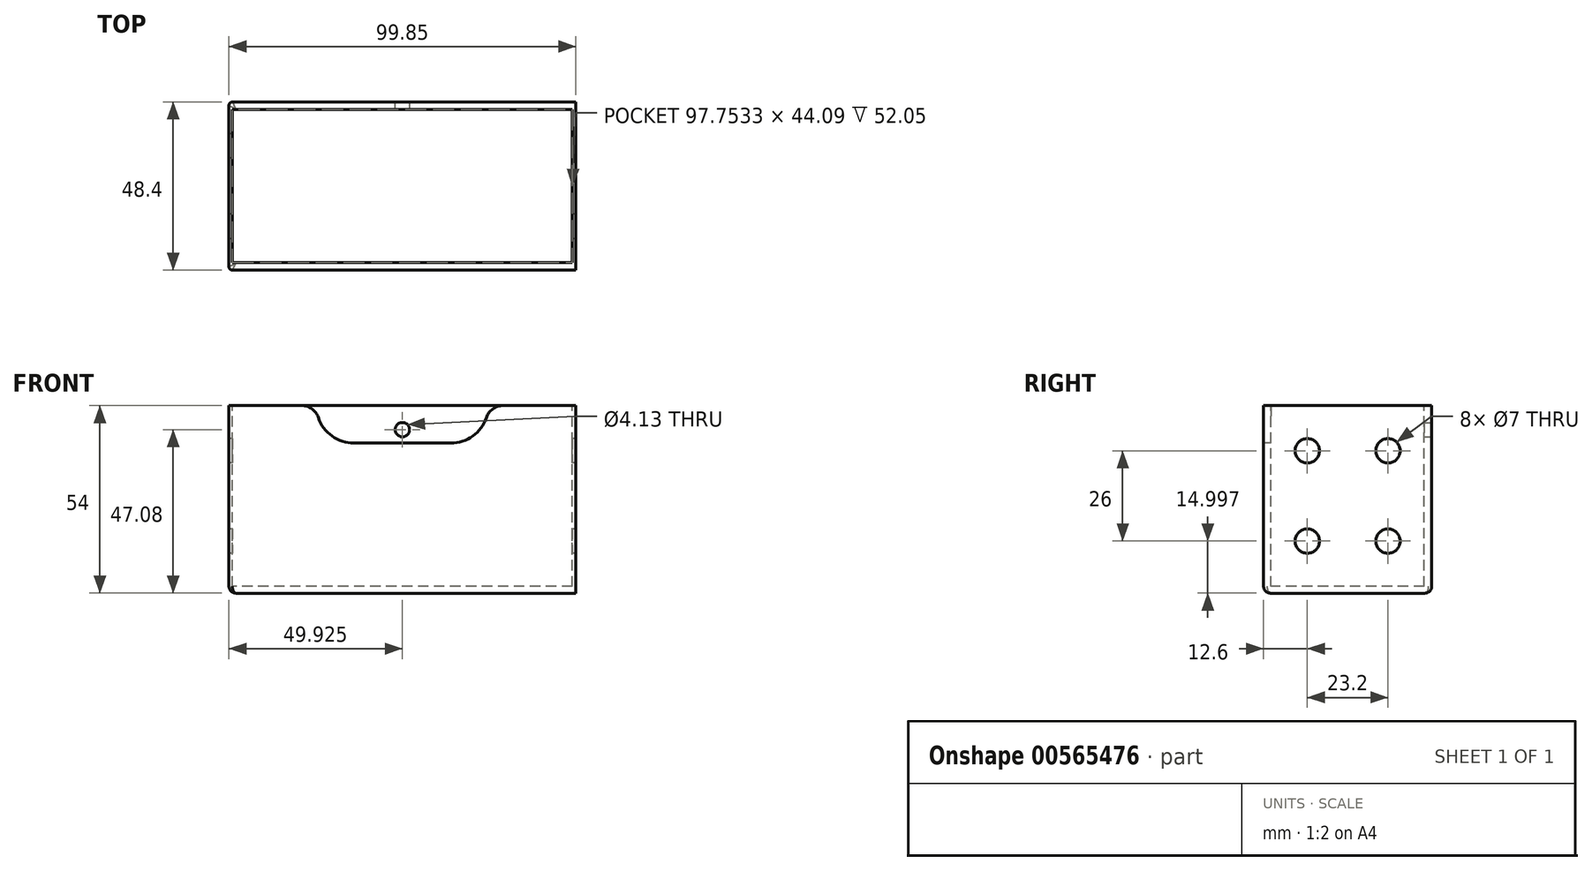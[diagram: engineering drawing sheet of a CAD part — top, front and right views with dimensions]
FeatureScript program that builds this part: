
annotation { "Feature Type Name" : "Feature", "Feature Type Description" : "" }
export const myFeature = defineFeature(function(context is Context, id is Id, definition is map)
    precondition{}
    {
        {
            var Q0;
            Q0=qCreatedBy(makeId("Front.planeOp"),FACE);
            var sketch = newSketch(context, id + "F0", { "sketchPlane" : qUnion([Q0])});
            skLineSegment(sketch, "E0.bottom", {"start": v(-48.42, 19.38) * mm, "end": v(51.43, 19.38) * mm});
            skLineSegment(sketch, "E0.top", {"start": v(-48.42, -34.62) * mm, "end": v(51.43, -34.62) * mm});
            skLineSegment(sketch, "E0.left", {"start": v(-48.42, 19.38) * mm, "end": v(-48.42, -34.62) * mm});
            skLineSegment(sketch, "E0.right", {"start": v(51.43, 19.38) * mm, "end": v(51.43, -34.62) * mm});
            skSolve(sketch);
        }
        {
            var Q0;
            Q0=makeQuery(id+"F0.imprint","IMPRINT",FACE,{"disambiguationData":[TD([[makeQuery(id+"F0.imprint","IMPRINT",EDGE,{"derivedFrom":sQuery(id+"F0.wireOp",EDGE,"E0.bottom")}),-1.0]])]});
            extrude(context, id + "F1", {"entities" : qUnion([Q0]), "depth" : (43.4 + 2 + 2 + 1) * mm, "offsetDistance" : 25 * mm});
        }
        {
            var Q0;
            Q0=makeQuery(id+"F1.opExtrude","SWEPT_FACE",FACE,{"disambiguationData":[OSD([sQuery(id+"F0.wireOp",EDGE,"E0.bottom")])]});
            var sketch = newSketch(context, id + "F2", { "sketchPlane" : qUnion([Q0])});
            skLineSegment(sketch, "E1.bottom", {"start": v(50.38, -2.15) * mm, "end": v(-47.37, -2.16) * mm});
            skLineSegment(sketch, "E1.top", {"start": v(50.38, -46.24) * mm, "end": v(-47.37, -46.25) * mm});
            skLineSegment(sketch, "E1.left", {"start": v(50.38, -2.15) * mm, "end": v(50.38, -46.24) * mm});
            skLineSegment(sketch, "E1.right", {"start": v(-47.37, -2.16) * mm, "end": v(-47.37, -46.25) * mm});
            skSolve(sketch);
        }
        {
            var Q0;
            Q0=makeQuery(id+"F1.opExtrude","SWEPT_FACE",FACE,{"disambiguationData":[OSD([sQuery(id+"F0.wireOp",EDGE,"E0.right")])]});
            extrude(context, id + "F3", {"entities" : qUnion([Q0]), "operationType" : NewBodyOperationType.ADD, "depth" : 1 * mm, "offsetDistance" : 25 * mm});
        }
        {
            var Q0;
            Q0=makeQuery(id+"F3.opExtrude","CAP_FACE",FACE,{"disambiguationData":[OSD([sQuery(id+"F0.wireOp",EDGE,"E0.right")])],"isStart":false});
            extrude(context, id + "F4", {"entities" : qUnion([Q0]), "operationType" : NewBodyOperationType.REMOVE, "oppositeDirection" : true, "depth" : 1 * mm, "offsetDistance" : 25 * mm});
        }
        {
            var Q0;
            Q0=makeQuery(id+"F2.imprint","IMPRINT",FACE,{"disambiguationData":[TD([[makeQuery(id+"F2.imprint","IMPRINT",EDGE,{"derivedFrom":sQuery(id+"F2.wireOp",EDGE,"E1.bottom")}),1.0]])]});
            extrude(context, id + "F5", {"entities" : qUnion([Q0]), "operationType" : NewBodyOperationType.REMOVE, "oppositeDirection" : true, "depth" : 52.05 * mm, "offsetDistance" : 25 * mm});
        }
        {
            var Q0;
            {var subQ0=sQuery(id+"F0.wireOp",EDGE,"E0.right");Q0=makeQuery(id+"F4.boolean.opBoolean","COPY",EDGE,{"derivedFrom":makeQuery(id+"F4.opExtrude","CAP_EDGE",EDGE,{"disambiguationData":[OSD([subQ0]),TDD([makeQuery(id+"F3.opExtrude","CAP_EDGE",EDGE,{"disambiguationData":[OSD([subQ0]),TDD([makeQuery(id+"F1.opExtrude","CAP_EDGE",EDGE,{"disambiguationData":[OSD([subQ0])],"isStart":false})])],"isStart":false})])],"isStart":false})});}
            var Q1;
            {var subQ0=sQuery(id+"F0.wireOp",EDGE,"E0.right");Q1=makeQuery(id+"F4.boolean.opBoolean","COPY",EDGE,{"derivedFrom":makeQuery(id+"F4.opExtrude","CAP_EDGE",EDGE,{"disambiguationData":[OSD([subQ0]),TDD([makeQuery(id+"F3.opExtrude","CAP_EDGE",EDGE,{"disambiguationData":[OSD([subQ0]),TDD([makeQuery(id+"F1.opExtrude","CAP_EDGE",EDGE,{"disambiguationData":[OSD([subQ0])],"isStart":true})])],"isStart":false})])],"isStart":false})});}
            var Q2;
            Q2=makeQuery(id+"F1.opExtrude","CAP_EDGE",EDGE,{"disambiguationData":[OSD([sQuery(id+"F0.wireOp",EDGE,"E0.left")])],"isStart":true});
            var Q3;
            Q3=makeQuery(id+"F1.opExtrude","CAP_EDGE",EDGE,{"disambiguationData":[OSD([sQuery(id+"F0.wireOp",EDGE,"E0.left")])],"isStart":false});
            fillet(context, id + "F6", {"entities" : qUnion([Q0, Q1, Q2, Q3]), "radius" : 1 * mm, "tangentPropagation" : true, "allowEdgeOverflow" : false});
        }
        {
            var Q0;
            {var subQ0=sQuery(id+"F0.wireOp",EDGE,"E0.right");var subQ1=sQuery(id+"F0.wireOp",EDGE,"E0.top");Q0=makeQuery(id+"F3.boolean.opBoolean","MERGE",EDGE,{"derivedFrom":[makeQuery(id+"F1.opExtrude","CAP_EDGE",EDGE,{"disambiguationData":[OSD([subQ1])],"isStart":false}),makeQuery(id+"F3.opExtrude","SWEPT_EDGE",EDGE,{"disambiguationData":[OSD([subQ1,subQ0]),TDD([makeQuery(id+"F1.opExtrude","CAP_VERTEX",VERTEX,{"disambiguationData":[OSD([subQ1,subQ0])],"isStart":false})])]})]});}
            var Q1;
            Q1=makeQuery(id+"F1.opExtrude","SWEPT_EDGE",EDGE,{"disambiguationData":[OSD([sQuery(id+"F0.wireOp",EDGE,"E0.top"),sQuery(id+"F0.wireOp",EDGE,"E0.left")])]});
            var Q2;
            {var subQ0=sQuery(id+"F0.wireOp",EDGE,"E0.right");var subQ1=sQuery(id+"F0.wireOp",EDGE,"E0.top");Q2=makeQuery(id+"F3.boolean.opBoolean","MERGE",EDGE,{"derivedFrom":[makeQuery(id+"F1.opExtrude","CAP_EDGE",EDGE,{"disambiguationData":[OSD([subQ1])],"isStart":true}),makeQuery(id+"F3.opExtrude","SWEPT_EDGE",EDGE,{"disambiguationData":[OSD([subQ1,subQ0]),TDD([makeQuery(id+"F1.opExtrude","CAP_VERTEX",VERTEX,{"disambiguationData":[OSD([subQ1,subQ0])],"isStart":true})])]})]});}
            var Q3;
            Q3=makeQuery(id+"F4.boolean.opBoolean","COPY",EDGE,{"derivedFrom":makeQuery(id+"F4.opExtrude","CAP_EDGE",EDGE,{"disambiguationData":[OSD([sQuery(id+"F0.wireOp",EDGE,"E0.top"),sQuery(id+"F0.wireOp",EDGE,"E0.right")])],"isStart":false})});
            fillet(context, id + "F7", {"entities" : qUnion([Q0, Q1, Q2, Q3]), "radius" : 2 * mm, "tangentPropagation" : true, "allowEdgeOverflow" : false});
        }
        {
            var Q0;
            {var subQ0=sQuery(id+"F0.wireOp",EDGE,"E0.right");Q0=makeQuery(id+"F3.boolean.opBoolean","MERGE",FACE,{"derivedFrom":[makeQuery(id+"F1.opExtrude","CAP_FACE",FACE,{"disambiguationData":[OSD([sQuery(id+"F0.wireOp",EDGE,"E0.bottom"),sQuery(id+"F0.wireOp",EDGE,"E0.top"),sQuery(id+"F0.wireOp",EDGE,"E0.left"),subQ0])],"isStart":false}),makeQuery(id+"F3.opExtrude","SWEPT_FACE",FACE,{"disambiguationData":[OSD([subQ0]),TDD([makeQuery(id+"F1.opExtrude","CAP_EDGE",EDGE,{"disambiguationData":[OSD([subQ0])],"isStart":false})])]})]});}
            var sketch = newSketch(context, id + "F8", { "sketchPlane" : qUnion([Q0])});
            skLineSegment(sketch, "E2", {"start": v(-47.42, 19.38) * mm, "end": v(50.43, 19.38) * mm});
            skCircle(sketch, "E3", {"center": v(-12.42, 19.38) * mm, "radius": 10.82 * mm});
            skCircle(sketch, "E4", {"center": v(15.43, 19.38) * mm, "radius": 10.82 * mm});
            skLineSegment(sketch, "E5", {"start": v(-12.42, 19.38) * mm, "end": v(-12.42, 8.56) * mm});
            skLineSegment(sketch, "E6", {"start": v(-12.42, 8.56) * mm, "end": v(15.43, 8.56) * mm});
            skLineSegment(sketch, "E7", {"start": v(15.43, 8.56) * mm, "end": v(15.43, 19.38) * mm});
            skSolve(sketch);
        }
        {
            var Q0;
            {var subQ0=sQuery(id+"F8.wireOp",EDGE,"E2");var subQ1=makeQuery(id+"F8.imprint","INTERSECT",VERTEX,{"derivedFrom":[subQ0,sQuery(id+"F8.wireOp",EDGE,"E5")]});Q0=makeQuery(id+"F8.imprint","IMPRINT",FACE,{"disambiguationData":[TD([[makeQuery(id+"F8.imprint","IMPRINT",EDGE,{"disambiguationData":[TD([[subQ1,1.0]])],"derivedFrom":subQ0}),1.0]])]});}
            var Q1;
            {var subQ0=sQuery(id+"F8.wireOp",EDGE,"E5");Q1=makeQuery(id+"F8.imprint","IMPRINT",FACE,{"disambiguationData":[TD([[makeQuery(id+"F8.imprint","IMPRINT",EDGE,{"derivedFrom":subQ0}),-1.0]])]});}
            var Q2;
            {var subQ0=sQuery(id+"F8.wireOp",EDGE,"E5");Q2=makeQuery(id+"F8.imprint","IMPRINT",FACE,{"disambiguationData":[TD([[makeQuery(id+"F8.imprint","IMPRINT",EDGE,{"derivedFrom":subQ0}),1.0]])]});}
            var Q3;
            {var subQ5=sQuery(id+"F8.wireOp",EDGE,"E6");Q3=makeQuery(id+"F8.imprint","IMPRINT",FACE,{"disambiguationData":[TD([[makeQuery(id+"F8.imprint","IMPRINT",EDGE,{"derivedFrom":subQ5}),1.0]])]});}
            var Q4;
            {var subQ0=sQuery(id+"F8.wireOp",EDGE,"E7");Q4=makeQuery(id+"F8.imprint","IMPRINT",FACE,{"disambiguationData":[TD([[makeQuery(id+"F8.imprint","IMPRINT",EDGE,{"derivedFrom":subQ0}),1.0]])]});}
            var Q5;
            {var subQ0=sQuery(id+"F8.wireOp",EDGE,"E7");Q5=makeQuery(id+"F8.imprint","IMPRINT",FACE,{"disambiguationData":[TD([[makeQuery(id+"F8.imprint","IMPRINT",EDGE,{"derivedFrom":subQ0}),-1.0]])]});}
            var Q6;
            {var subQ0=sQuery(id+"F8.wireOp",EDGE,"E2");var subQ1=makeQuery(id+"F8.imprint","INTERSECT",VERTEX,{"derivedFrom":[subQ0,sQuery(id+"F8.wireOp",EDGE,"E7")]});Q6=makeQuery(id+"F8.imprint","IMPRINT",FACE,{"disambiguationData":[TD([[makeQuery(id+"F8.imprint","IMPRINT",EDGE,{"disambiguationData":[TD([[subQ1,1.0]])],"derivedFrom":subQ0}),1.0]])]});}
            extrude(context, id + "F9", {"entities" : qUnion([Q0, Q1, Q2, Q3, Q4, Q5, Q6]), "operationType" : NewBodyOperationType.REMOVE, "oppositeDirection" : true, "depth" : 25 * mm, "offsetDistance" : 25 * mm});
        }
        {
            var Q0;
            {var subQ0=sQuery(id+"F0.wireOp",EDGE,"E0.right");Q0=makeQuery(id+"F3.boolean.opBoolean","MERGE",FACE,{"derivedFrom":[makeQuery(id+"F1.opExtrude","CAP_FACE",FACE,{"disambiguationData":[OSD([sQuery(id+"F0.wireOp",EDGE,"E0.bottom"),sQuery(id+"F0.wireOp",EDGE,"E0.top"),sQuery(id+"F0.wireOp",EDGE,"E0.left"),subQ0])],"isStart":true}),makeQuery(id+"F3.opExtrude","SWEPT_FACE",FACE,{"disambiguationData":[OSD([subQ0]),TDD([makeQuery(id+"F1.opExtrude","CAP_EDGE",EDGE,{"disambiguationData":[OSD([subQ0])],"isStart":true})])]})]});}
            var sketch = newSketch(context, id + "F10", { "sketchPlane" : qUnion([Q0])});
            skCircle(sketch, "E8", {"center": v(-1.5, 12.46) * mm, "radius": 2.06 * mm});
            skPoint(sketch, "E8.centerSnap0", {"position": v(-1.5, 19.38) * mm});
            skSolve(sketch);
        }
        {
            var Q0;
            Q0 = qSketchRegion(id + "F10", true);
            extrude(context, id + "F11", {"entities" : qUnion([Q0]), "operationType" : NewBodyOperationType.REMOVE, "oppositeDirection" : true, "depth" : 25 * mm, "offsetDistance" : 25 * mm});
        }
        {
            var Q0;
            Q0=makeQuery(id+"F1.opExtrude","SWEPT_FACE",FACE,{"disambiguationData":[OSD([sQuery(id+"F0.wireOp",EDGE,"E0.left")])]});
            var sketch = newSketch(context, id + "F12", { "sketchPlane" : qUnion([Q0])});
            skLineSegment(sketch, "E9", {"start": v(47.4, -32.62) * mm, "end": v(47.4, 19.38) * mm});
            skCircle(sketch, "E10", {"center": v(12.6, 6.38) * mm, "radius": 3.5 * mm});
            skCircle(sketch, "E11", {"center": v(35.8, 6.38) * mm, "radius": 3.5 * mm});
            skCircle(sketch, "E12", {"center": v(35.8, -19.62) * mm, "radius": 3.5 * mm});
            skCircle(sketch, "E13", {"center": v(12.6, -19.62) * mm, "radius": 3.5 * mm});
            skSolve(sketch);
        }
        {
            var Q0;
            Q0 = qSketchRegion(id + "F12", true);
            extrude(context, id + "F13", {"entities" : qUnion([Q0]), "operationType" : NewBodyOperationType.REMOVE, "oppositeDirection" : true, "depth" : 125.8 * mm, "offsetDistance" : 25 * mm});
        }
        {
            var Q0;
            {var subQ0=sQuery(id+"F0.wireOp",EDGE,"E0.bottom");Q0=makeQuery(id+"F9.boolean.opBoolean","INTERSECT",EDGE,{"derivedFrom":[makeQuery(id+"F3.boolean.opBoolean","MERGE",FACE,{"derivedFrom":[makeQuery(id+"F1.opExtrude","SWEPT_FACE",FACE,{"disambiguationData":[OSD([subQ0])]}),makeQuery(id+"F3.opExtrude","SWEPT_FACE",FACE,{"disambiguationData":[OSD([subQ0,sQuery(id+"F0.wireOp",EDGE,"E0.right")])]})]}),makeQuery(id+"F9.opExtrude","SWEPT_FACE",FACE,{"disambiguationData":[OSD([sQuery(id+"F8.wireOp",EDGE,"E4")])]})]});}
            var Q1;
            {var subQ0=sQuery(id+"F0.wireOp",EDGE,"E0.bottom");Q1=makeQuery(id+"F9.boolean.opBoolean","INTERSECT",EDGE,{"derivedFrom":[makeQuery(id+"F3.boolean.opBoolean","MERGE",FACE,{"derivedFrom":[makeQuery(id+"F1.opExtrude","SWEPT_FACE",FACE,{"disambiguationData":[OSD([subQ0])]}),makeQuery(id+"F3.opExtrude","SWEPT_FACE",FACE,{"disambiguationData":[OSD([subQ0,sQuery(id+"F0.wireOp",EDGE,"E0.right")])]})]}),makeQuery(id+"F9.opExtrude","SWEPT_FACE",FACE,{"disambiguationData":[OSD([sQuery(id+"F8.wireOp",EDGE,"E3")])]})]});}
            fillet(context, id + "F14", {"entities" : qUnion([Q0, Q1]), "radius" : 5 * mm, "tangentPropagation" : true, "allowEdgeOverflow" : false});
        }
    });
